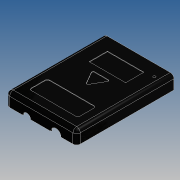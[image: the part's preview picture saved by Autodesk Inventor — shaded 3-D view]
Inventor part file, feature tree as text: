
AUTODESK INVENTOR PART (.ipt)
format: ipt  version: 2015 SP1 (Build 190203100, 203)  size: 369,152 bytes
history: native  units: mm
features: fillet x7, sketch x7, extrude x6, mirror x2, shell x1, hole x1
ambient origin geometry x8: Origin, YZ Plane, XZ Plane, XY Plane, X Axis, Y Axis, Z Axis, Center Point
bodies: Solid1 (feature_tree)
feature tree (24):
  extrude  "Extrusion1"  Depth=40.0mm
  shell  "Shell1"  Thickness=11.0mm
  extrude  "Extrusion2"  Depth=1.0mm
  extrude  "Extrusion3"  Depth=10.0mm
  fillet  "Fillet3"  Radius=20.0mm
  mirror  "Mirror1"
  mirror  "Mirror2"
  fillet  "Fillet4"  Radius=0.2mm
  fillet  "Fillet5"  Radius=5.0mm
  fillet  "Fillet6"  Radius=0.2mm
  extrude  "Extrusion4"  Depth=0.2mm
  extrude  "Extrusion6"  Depth=1.0mm
  fillet  "Fillet7"  Radius=3.0mm
  hole  "Hole1"  [1 undecoded]
  extrude  "Extrusion7"  Depth=4.2mm
  fillet  "Fillet8"  Radius=3.2mm
  fillet  "Fillet9"  Radius=10.0mm
  sketch  "Sketch1"  dims[d0=29.0mm d1=40.0mm d2=11.0mm d3=0.0mm]
  sketch  "Sketch2"  dims[d6=2.0mm d7=1.0mm]
  sketch  "Sketch3"  dims[d8=2.0mm d9=0.0mm d10=10.0mm d11=20.0mm d12=0.2mm d13=5.0mm d14=0.2mm]
  sketch  "Sketch4"  dims[d15=0.8mm d16=0.0mm d17=0.2mm]
  sketch  "Sketch5"  dims[d18=1.0mm d19=1.0mm d20=3.0mm]
  sketch  "Sketch6"  dims[d21=3.0mm d22=12.0mm]
  sketch  "Sketch7"  dims[d23=12.0mm d24=4.2mm d25=3.2mm d26=10.0mm d27=0.0mm d32=2.0mm d33=3.0mm d34=10.0mm d35=0.0mm d36=2.0mm d37=6.5mm d38=9.6mm d39=2.0mm d40=6.0mm d41=4.0mm d42=2.0mm d43=90.0deg d44=8.0mm d45=20.594885mm d46=40.0mm d47=15.0mm d48=10.0mm d49=15.0mm d51=5.0mm d52=30.0mm d53=15.0mm d54=5.0mm d55=0.4mm d56=0.0mm d57=2.0mm d58=1.0mm]
note: 1 required parameter value undecoded (feature->parameter linkage not recoverable at this tier; creation-order binding heuristic only, values carry confidence <= 0.55)
